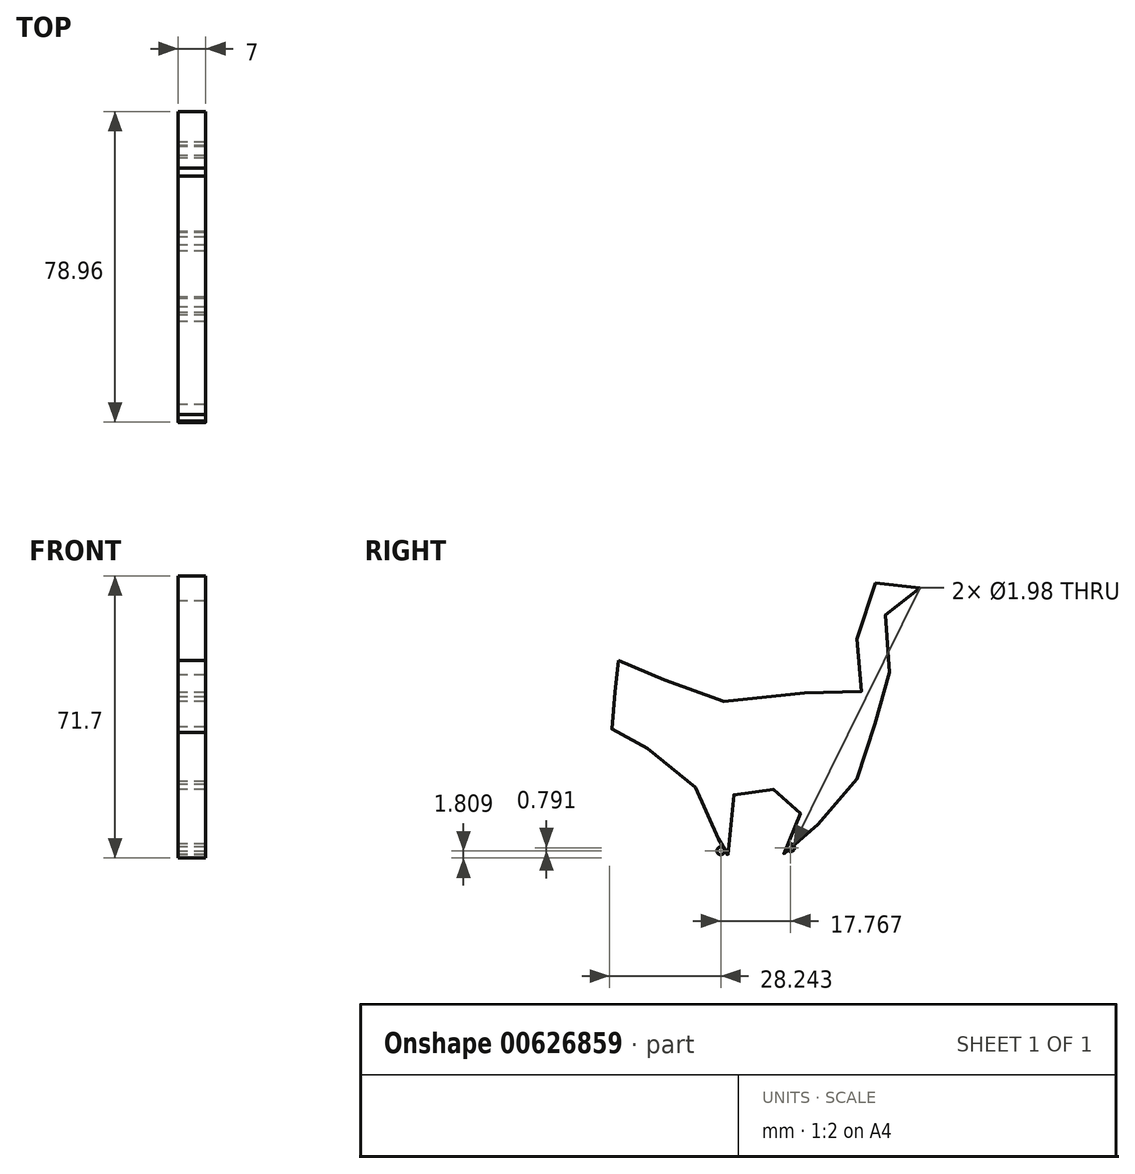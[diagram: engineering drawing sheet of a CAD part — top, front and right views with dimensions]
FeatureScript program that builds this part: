
annotation { "Feature Type Name" : "Feature", "Feature Type Description" : "" }
export const myFeature = defineFeature(function(context is Context, id is Id, definition is map)
    precondition{}
    {
        {
            var Q0;
            Q0=qCreatedBy(makeId("Right.planeOp"),FACE);
            var sketch = newSketch(context, id + "F0", { "sketchPlane" : qUnion([Q0])});
            skLineSegment(sketch, "E0.bottom", {"start": v(-40.96, 35.64) * mm, "end": v(39.04, 35.64) * mm});
            skLineSegment(sketch, "E0.top", {"start": v(-40.96, -44.36) * mm, "end": v(39.04, -44.36) * mm});
            skLineSegment(sketch, "E0.left", {"start": v(-40.96, 35.64) * mm, "end": v(-40.96, -44.36) * mm});
            skLineSegment(sketch, "E0.right", {"start": v(39.04, 35.64) * mm, "end": v(39.04, -44.36) * mm});
            skFitSpline(sketch, "E1", {"points": [v(-37.98, 13.56) * mm, v(-38.17, 12.76) * mm, v(-37.64, 11.29) * mm, v(-36.65, 9.8) * mm, v(-35.74, 8.48) * mm, v(-36.2, 7.84) * mm, v(-37.67, 6.93) * mm, v(-39.11, 5.07) * mm, v(-39.68, 3.52) * mm, v(-39.83, 1.36) * mm, v(-39.83, -0.42) * mm, v(-39.76, -1.52) * mm, v(-40.17, -2.84) * mm, v(-40.02, -3.45) * mm, v(-38.77, -4.36) * mm, v(-36.88, -4.66) * mm, v(-35.21, -3.9) * mm, v(-34.64, -3.3) * mm, v(-33.05, -5.12) * mm, v(-30.63, -8.75) * mm, v(-28.66, -11.33) * mm, v(-26.39, -13.87) * mm, v(-22.3, -16.48) * mm, v(-18.54, -18.49) * mm, v(-16.23, -20.46) * mm, v(-14.72, -23.6) * mm, v(-13.77, -27.09) * mm, v(-12.86, -30.42) * mm, v(-12.4, -32.62) * mm, v(-12.33, -33.07) * mm, v(-12.67, -33.19) * mm, v(-14.23, -34.63) * mm, v(-14.5, -35.69) * mm, v(-13.32, -36.25) * mm, v(-11.27, -36.52) * mm, v(-9.9, -35.46) * mm, v(-9.23, -33.87) * mm, v(-8.7, -31.67) * mm, v(-8.47, -27.5) * mm, v(-8.5, -22.24) * mm, v(-8.73, -17.16) * mm, v(-8.54, -17.16) * mm, v(-6.65, -18) * mm, v(-4.07, -18.75) * mm, v(-0.7, -19.1) * mm, v(3.2, -19.06) * mm, v(5.93, -18.6) * mm, v(8.12, -17.88) * mm, v(8.09, -18.07) * mm, v(8.2, -21.44) * mm, v(8.2, -26.6) * mm, v(7.33, -30.3) * mm, v(5.93, -31.48) * mm, v(4.41, -32.62) * mm, v(3.35, -34.17) * mm, v(3.77, -35.27) * mm, v(5.24, -35.72) * mm, v(6.99, -35.3) * mm, v(8.65, -34.2) * mm, v(11.27, -31.22) * mm, v(11.84, -29.9) * mm, v(13.46, -26.7) * mm, v(15.36, -23.8) * mm, v(17.78, -21.14) * mm, v(20.55, -18.64) * mm, v(22.94, -16.1) * mm, v(24.98, -12.39) * mm, v(26.15, -9.59) * mm, v(27.33, -5.34) * mm, v(27.52, -4.2) * mm, v(26.95, -0.5) * mm, v(27.48, 0) * mm, v(29.72, 3.45) * mm, v(30.7, 7.35) * mm, v(30.9, 9.01) * mm, v(31, 13.9) * mm, v(30.74, 17.84) * mm, v(30.13, 20) * mm, v(30.06, 22.5) * mm, v(29.9, 25.5) * mm, v(30.47, 27.42) * mm, v(32.14, 28.67) * mm, v(35.55, 28.83) * mm, v(38.47, 30.34) * mm, v(38.7, 31.82) * mm, v(37.63, 33.64) * mm, v(35.51, 34.92) * mm, v(32.75, 35.08) * mm, v(30.28, 34.58) * mm, v(27.75, 33.45) * mm, v(25.59, 31.82) * mm, v(24.07, 29.2) * mm, v(22.67, 25.6) * mm, v(22.4, 20.45) * mm, v(23.28, 16.55) * mm, v(24, 13.1) * mm, v(24.37, 9.77) * mm, v(24.41, 8.64) * mm, v(23.96, 6.32) * mm, v(23.2, 4.66) * mm, v(21.72, 4.43) * mm, v(19.49, 4.88) * mm, v(15.32, 5.45) * mm, v(8.77, 5.34) * mm, v(2.37, 5) * mm, v(-4.57, 3.86) * mm, v(-10.78, 3.22) * mm, v(-17.1, 3.4) * mm, v(-20.33, 4.24) * mm, v(-23.28, 5.98) * mm, v(-26.31, 8.64) * mm, v(-29.04, 9.89) * mm, v(-31.58, 10.07) * mm, v(-32.64, 11.36) * mm, v(-34.95, 12.84) * mm, v(-37.98, 13.56) * mm]});
            skSolve(sketch);
        }
        {
            var Q0;
            Q0=makeQuery(id+"F0.imprint","IMPRINT",FACE,{"disambiguationData":[TD([[makeQuery(id+"F0.imprint","IMPRINT",EDGE,{"derivedFrom":sQuery(id+"F0.wireOp",EDGE,"E1")}),1.0]])]});
            extrude(context, id + "F1", {"entities" : qUnion([Q0]), "depth" : 7 * mm, "offsetDistance" : 25 * mm});
        }
        {
            var Q0;
            Q0=qCreatedBy(makeId("Right.planeOp"),FACE);
            var sketch = newSketch(context, id + "F2", { "sketchPlane" : qUnion([Q0])});
            skCircle(sketch, "E2", {"center": v(-11.95, -34.76) * mm, "radius": 0.99 * mm});
            skCircle(sketch, "E3", {"center": v(5.82, -33.97) * mm, "radius": 0.99 * mm});
            skSolve(sketch);
        }
        {
            var Q0;
            Q0=makeQuery(id+"F2.imprint","IMPRINT",FACE,{"disambiguationData":[TD([[makeQuery(id+"F2.imprint","IMPRINT",EDGE,{"derivedFrom":sQuery(id+"F2.wireOp",EDGE,"E2")}),1.0]])]});
            var Q1;
            Q1=makeQuery(id+"F2.imprint","IMPRINT",FACE,{"disambiguationData":[TD([[makeQuery(id+"F2.imprint","IMPRINT",EDGE,{"derivedFrom":sQuery(id+"F2.wireOp",EDGE,"E3")}),1.0]])]});
            var Q2;
            Q2=sQuery(id+"F2.wireOp",EDGE,"E2");
            extrude(context, id + "F3", {"entities" : qUnion([Q0, Q1]), "operationType" : NewBodyOperationType.REMOVE, "surfaceEntities" : qUnion([Q2]), "endBound" : BoundingType.THROUGH_ALL, "depth" : 25 * mm, "offsetDistance" : 25 * mm});
        }
    });
